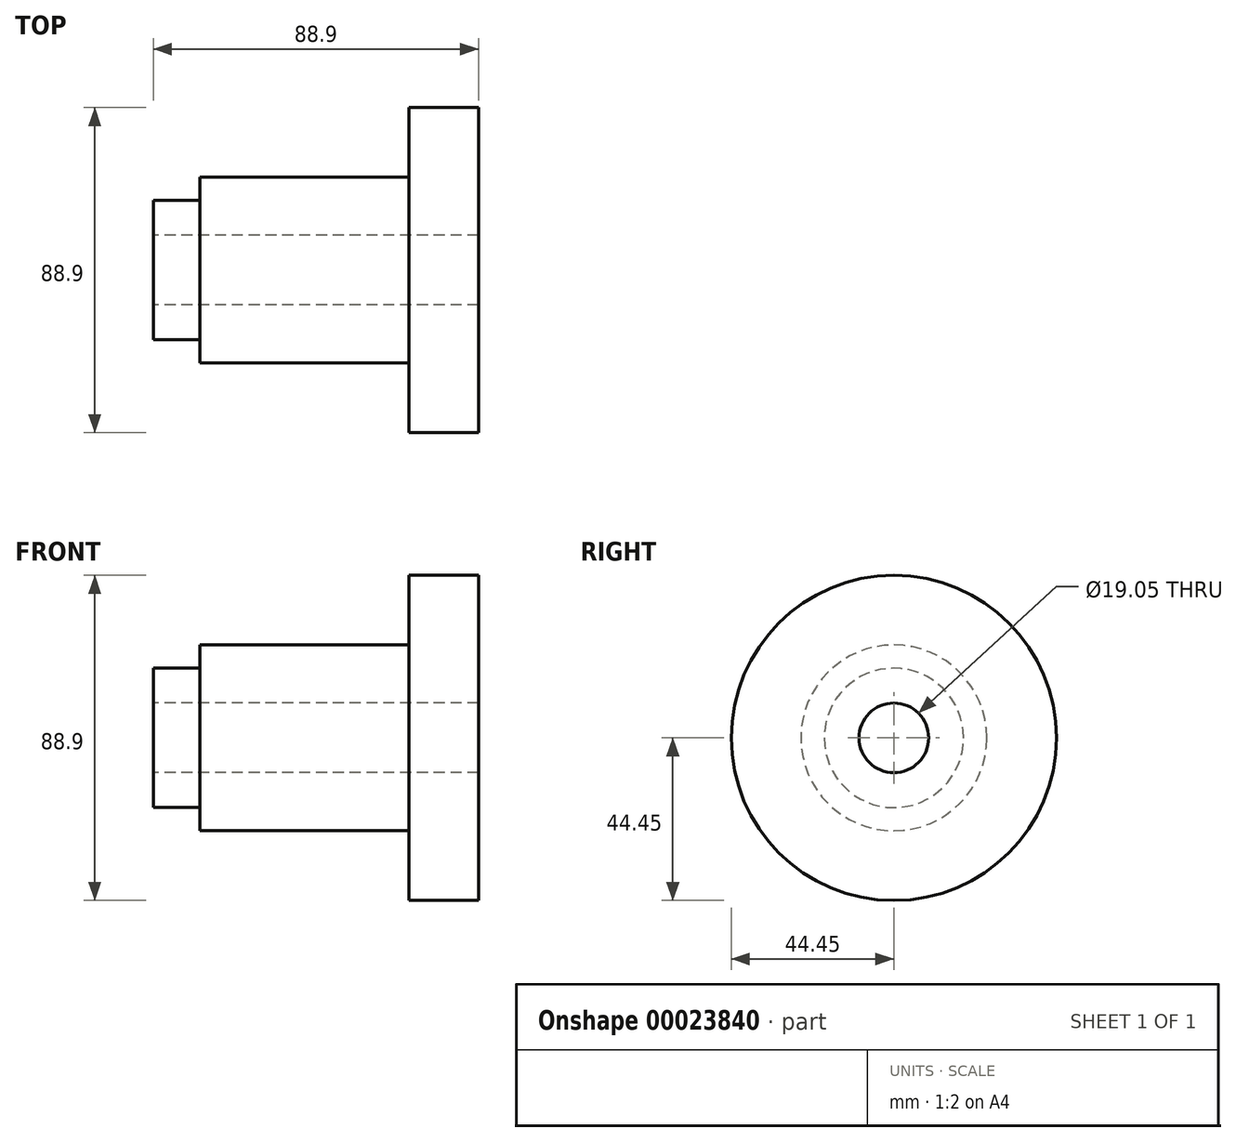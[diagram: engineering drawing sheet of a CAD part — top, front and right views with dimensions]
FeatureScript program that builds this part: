
annotation { "Feature Type Name" : "Feature", "Feature Type Description" : "" }
export const myFeature = defineFeature(function(context is Context, id is Id, definition is map)
    precondition{}
    {
        {
            var Q0;
            Q0=qCreatedBy(makeId("Front.planeOp"),FACE);
            var sketch = newSketch(context, id + "F0", { "sketchPlane" : qUnion([Q0])});
            skLineSegment(sketch, "E0", {"start": v(2.9, 0) * mm, "end": v(-88.9, 0) * mm, "construction": true});
            skLineSegment(sketch, "E1.bottom", {"start": v(-88.9, 0) * mm, "end": v(-76.2, 0) * mm});
            skLineSegment(sketch, "E1.top", {"start": v(-88.9, 19.05) * mm, "end": v(-76.2, 19.05) * mm});
            skLineSegment(sketch, "E1.left", {"start": v(-88.9, 0) * mm, "end": v(-88.9, 19.05) * mm});
            skLineSegment(sketch, "E1.right", {"start": v(-76.2, 0) * mm, "end": v(-76.2, 19.05) * mm});
            skLineSegment(sketch, "E2.bottom", {"start": v(-76.2, 0) * mm, "end": v(-19.05, 0) * mm});
            skLineSegment(sketch, "E2.top", {"start": v(-76.2, 25.4) * mm, "end": v(-19.05, 25.4) * mm});
            skLineSegment(sketch, "E2.left", {"start": v(-76.2, 0) * mm, "end": v(-76.2, 25.4) * mm});
            skLineSegment(sketch, "E2.right", {"start": v(-19.05, 0) * mm, "end": v(-19.05, 25.4) * mm});
            skLineSegment(sketch, "E3.bottom", {"start": v(-19.05, 0) * mm, "end": v(0, 0) * mm});
            skLineSegment(sketch, "E3.top", {"start": v(-19.05, 44.45) * mm, "end": v(0, 44.45) * mm});
            skLineSegment(sketch, "E3.left", {"start": v(-19.05, 0) * mm, "end": v(-19.05, 44.45) * mm});
            skLineSegment(sketch, "E3.right", {"start": v(0, 0) * mm, "end": v(0, 44.45) * mm});
            skSolve(sketch);
        }
        {
            var Q0;
            {var subQ2=sQuery(id+"F0.wireOp",EDGE,"E1.bottom");Q0=makeQuery(id+"F0.imprint","IMPRINT",FACE,{"disambiguationData":[TD([[makeQuery(id+"F0.imprint","IMPRINT",EDGE,{"derivedFrom":subQ2}),1.0]])]});}
            var Q1;
            {var subQ3=sQuery(id+"F0.wireOp",EDGE,"E3.bottom");Q1=makeQuery(id+"F0.imprint","IMPRINT",FACE,{"disambiguationData":[TD([[makeQuery(id+"F0.imprint","IMPRINT",EDGE,{"derivedFrom":subQ3}),1.0]])]});}
            var Q2;
            {var subQ2=sQuery(id+"F0.wireOp",EDGE,"E2.bottom");Q2=makeQuery(id+"F0.imprint","IMPRINT",FACE,{"disambiguationData":[TD([[makeQuery(id+"F0.imprint","IMPRINT",EDGE,{"derivedFrom":subQ2}),1.0]])]});}
            var Q3;
            Q3=sQuery(id+"F0.wireOp",EDGE,"E2.bottom");
            revolve(context, id + "F1", {"entities" : qUnion([Q0, Q1, Q2]), "axis" : qUnion([Q3]), "revolveType" : RevolveType.FULL});
        }
        {
            var Q0;
            Q0=makeQuery(id+"F1.opRevolve","SWEPT_FACE",FACE,{"disambiguationData":[OSD([sQuery(id+"F0.wireOp",EDGE,"E1.left")])]});
            var sketch = newSketch(context, id + "F2", { "sketchPlane" : qUnion([Q0])});
            skCircle(sketch, "E4", {"center": v(0, 0) * mm, "radius": 9.53 * mm});
            skLineSegment(sketch, "E5", {"start": v(0, 0) * mm, "end": v(-40.83, 0) * mm});
            skLineSegment(sketch, "E6", {"start": v(-40.83, 0) * mm, "end": v(44.8, 0) * mm});
            skSolve(sketch);
        }
        {
            var Q0;
            Q0 = qSketchRegion(id + "F2", true);
            extrude(context, id + "F3", {"entities" : qUnion([Q0]), "operationType" : NewBodyOperationType.REMOVE, "endBound" : BoundingType.THROUGH_ALL, "oppositeDirection" : true, "depth" : 25.4 * mm});
        }
    });
